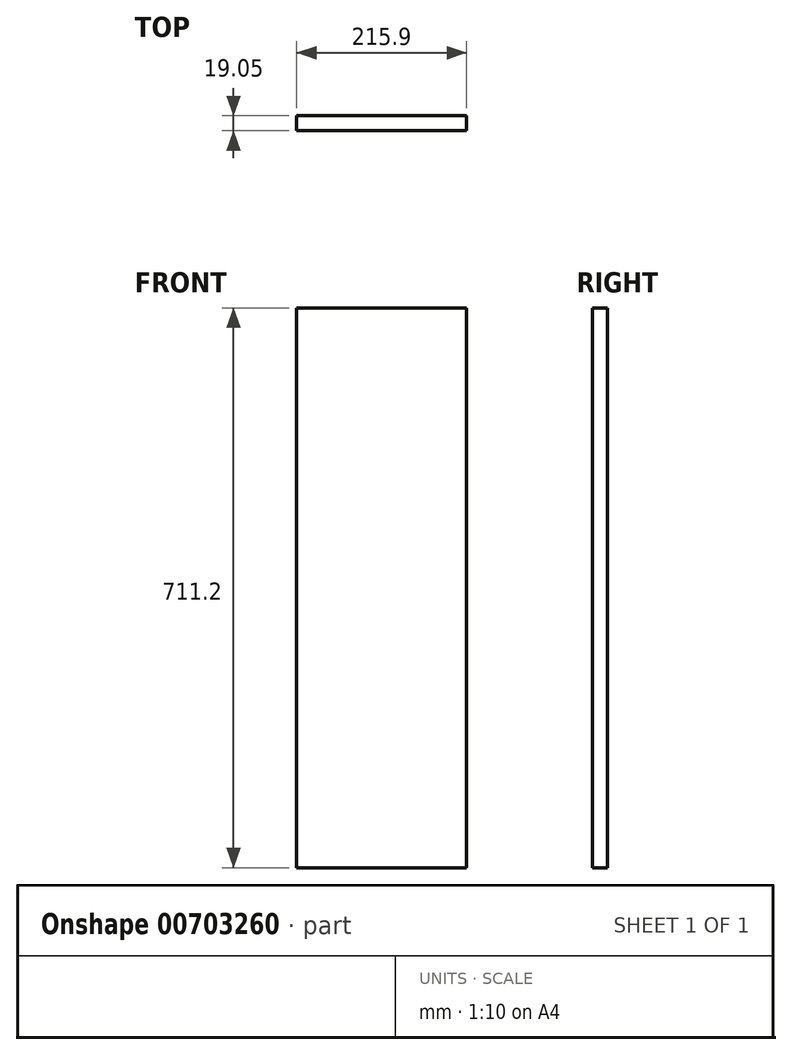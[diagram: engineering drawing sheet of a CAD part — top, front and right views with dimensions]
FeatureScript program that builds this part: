
annotation { "Feature Type Name" : "Feature", "Feature Type Description" : "" }
export const myFeature = defineFeature(function(context is Context, id is Id, definition is map)
    precondition{}
    {
        {
            var Q0;
            Q0=qCreatedBy(makeId("Front.planeOp"),FACE);
            var sketch = newSketch(context, id + "F0", { "sketchPlane" : qUnion([Q0])});
            skLineSegment(sketch, "E0.bottom", {"start": v(-107.95, 355.6) * mm, "end": v(107.95, 355.6) * mm});
            skLineSegment(sketch, "E0.top", {"start": v(-107.95, -355.6) * mm, "end": v(107.95, -355.6) * mm});
            skLineSegment(sketch, "E0.left", {"start": v(-107.95, 355.6) * mm, "end": v(-107.95, -355.6) * mm});
            skLineSegment(sketch, "E0.right", {"start": v(107.95, 355.6) * mm, "end": v(107.95, -355.6) * mm});
            skPoint(sketch, "E0.middle", {"position": v(0, 0) * mm});
            skSolve(sketch);
        }
        {
            var Q0;
            Q0=makeQuery(id+"F0.imprint","IMPRINT",FACE,{"disambiguationData":[TD([[makeQuery(id+"F0.imprint","IMPRINT",EDGE,{"derivedFrom":sQuery(id+"F0.wireOp",EDGE,"E0.bottom")}),-1.0]])]});
            extrude(context, id + "F1", {"entities" : qUnion([Q0]), "depth" : 19.05 * mm, "offsetDistance" : 25.4 * mm});
        }
    });
